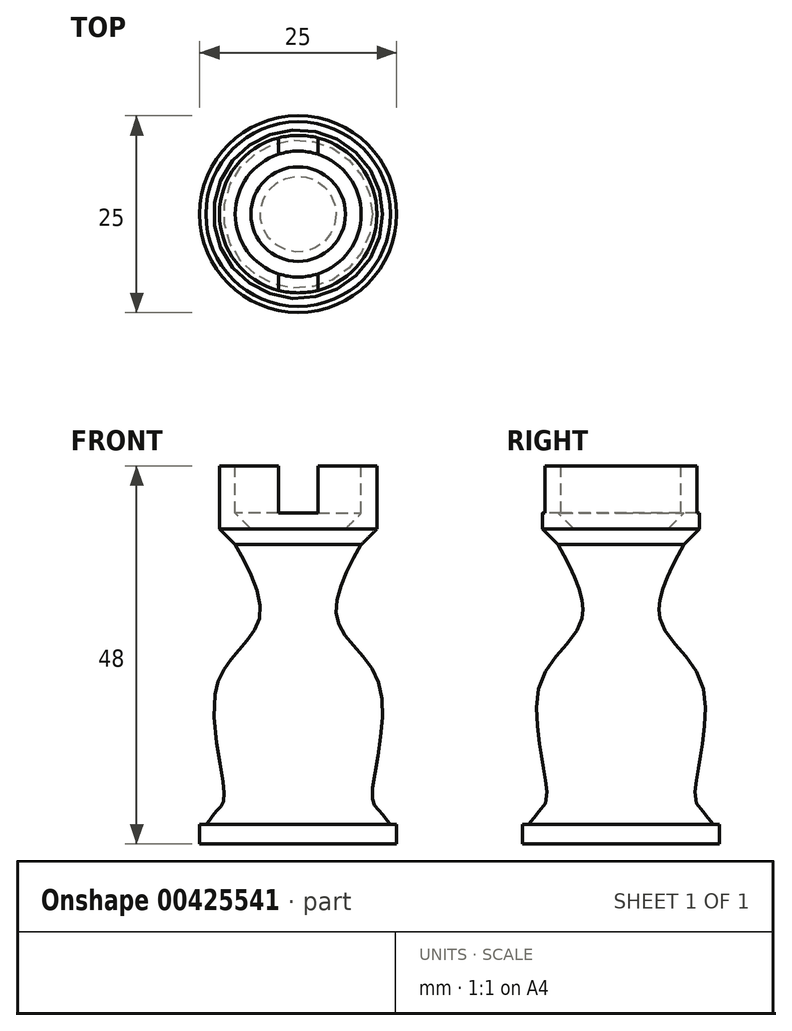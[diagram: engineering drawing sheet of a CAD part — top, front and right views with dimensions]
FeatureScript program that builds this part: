
annotation { "Feature Type Name" : "Feature", "Feature Type Description" : "" }
export const myFeature = defineFeature(function(context is Context, id is Id, definition is map)
    precondition{}
    {
        {
            var Q0;
            Q0=qCreatedBy(makeId("Front.planeOp"),FACE);
            var sketch = newSketch(context, id + "F0", { "sketchPlane" : qUnion([Q0])});
            skLineSegment(sketch, "E0.bottom", {"start": v(0, 0) * mm, "end": v(12.5, 0) * mm});
            skLineSegment(sketch, "E0.top", {"start": v(0, 48) * mm, "end": v(12.5, 48) * mm});
            skLineSegment(sketch, "E0.left", {"start": v(0, 0) * mm, "end": v(0, 48) * mm});
            skLineSegment(sketch, "E0.right", {"start": v(12.5, 0) * mm, "end": v(12.5, 48) * mm});
            skLineSegment(sketch, "E1.bottom", {"start": v(0, 48) * mm, "end": v(8, 48) * mm});
            skLineSegment(sketch, "E1.top", {"start": v(0, 40) * mm, "end": v(8, 40) * mm});
            skLineSegment(sketch, "E1.left", {"start": v(0, 48) * mm, "end": v(0, 40) * mm});
            skLineSegment(sketch, "E1.right", {"start": v(8, 48) * mm, "end": v(8, 40) * mm});
            skLineSegment(sketch, "E2", {"start": v(10, 48) * mm, "end": v(10, 38) * mm});
            skLineSegment(sketch, "E3", {"start": v(10, 38) * mm, "end": v(0, 38) * mm});
            skLineSegment(sketch, "E4", {"start": v(10, 40) * mm, "end": v(8, 38) * mm});
            skLineSegment(sketch, "E5", {"start": v(0, 2.5) * mm, "end": v(12.5, 2.5) * mm});
            skPoint(sketch, "E6.1.internal.snap0", {"position": v(5, 38) * mm});
            skFitSpline(sketch, "E6", {"points": [v(8, 38) * mm, v(5, 28.35) * mm, v(10.38, 19.98) * mm, v(9.44, 5.69) * mm, v(10.5, 4.05) * mm, v(11.73, 2.5) * mm], "startDerivative": vector(-21.67, -38.09) * mm, "endDerivative": vector(9.4, -5.83) * mm});
            skSolve(sketch);
        }
        {
            var Q0;
            {var subQ0=sQuery(id+"F0.wireOp",EDGE,"E1.top");Q0=makeQuery(id+"F0.imprint","IMPRINT",FACE,{"disambiguationData":[TD([[makeQuery(id+"F0.imprint","IMPRINT",EDGE,{"derivedFrom":subQ0}),-1.0]])]});}
            var Q1;
            {var subQ5=sQuery(id+"F0.wireOp",EDGE,"E6");Q1=makeQuery(id+"F0.imprint","IMPRINT",FACE,{"disambiguationData":[TD([[makeQuery(id+"F0.imprint","IMPRINT",EDGE,{"derivedFrom":subQ5}),-1.0]])]});}
            var Q2;
            {var subQ5=sQuery(id+"F0.wireOp",EDGE,"E0.bottom");Q2=makeQuery(id+"F0.imprint","IMPRINT",FACE,{"disambiguationData":[TD([[makeQuery(id+"F0.imprint","IMPRINT",EDGE,{"derivedFrom":subQ5}),1.0]])]});}
            var Q3;
            Q3=sQuery(id+"F0.wireOp",EDGE,"E1.left");
            revolve(context, id + "F1", {"entities" : qUnion([Q0, Q1, Q2]), "axis" : qUnion([Q3]), "revolveType" : RevolveType.FULL});
        }
        {
            var Q0;
            Q0=makeQuery(id+"F1.opRevolve","SWEPT_FACE",FACE,{"disambiguationData":[OSD([sQuery(id+"F0.wireOp",EDGE,"E0.top")])]});
            var sketch = newSketch(context, id + "F2", { "sketchPlane" : qUnion([Q0])});
            skLineSegment(sketch, "E7.bottom", {"start": v(-2.5, 15) * mm, "end": v(2.5, 15) * mm});
            skLineSegment(sketch, "E7.top", {"start": v(-2.5, -15) * mm, "end": v(2.5, -15) * mm});
            skLineSegment(sketch, "E7.left", {"start": v(-2.5, 15) * mm, "end": v(-2.5, -15) * mm});
            skLineSegment(sketch, "E7.right", {"start": v(2.5, 15) * mm, "end": v(2.5, -15) * mm});
            skPoint(sketch, "E7.middle", {"position": v(0, 0) * mm});
            skSolve(sketch);
        }
        {
            var Q0;
            Q0 = qSketchRegion(id + "F2", true);
            extrude(context, id + "F3", {"entities" : qUnion([Q0]), "operationType" : NewBodyOperationType.REMOVE, "oppositeDirection" : true, "depth" : 6 * mm});
        }
        {
            var Q0;
            Q0=makeQuery(id+"F1.opRevolve","SWEPT_EDGE",EDGE,{"disambiguationData":[OSD([sQuery(id+"F0.wireOp",EDGE,"E1.top"),sQuery(id+"F0.wireOp",EDGE,"E1.right")])]});
            chamfer(context, id + "F4", {"entities" : qUnion([Q0]), "width" : 2 * mm, "tangentPropagation" : true});
        }
    });
